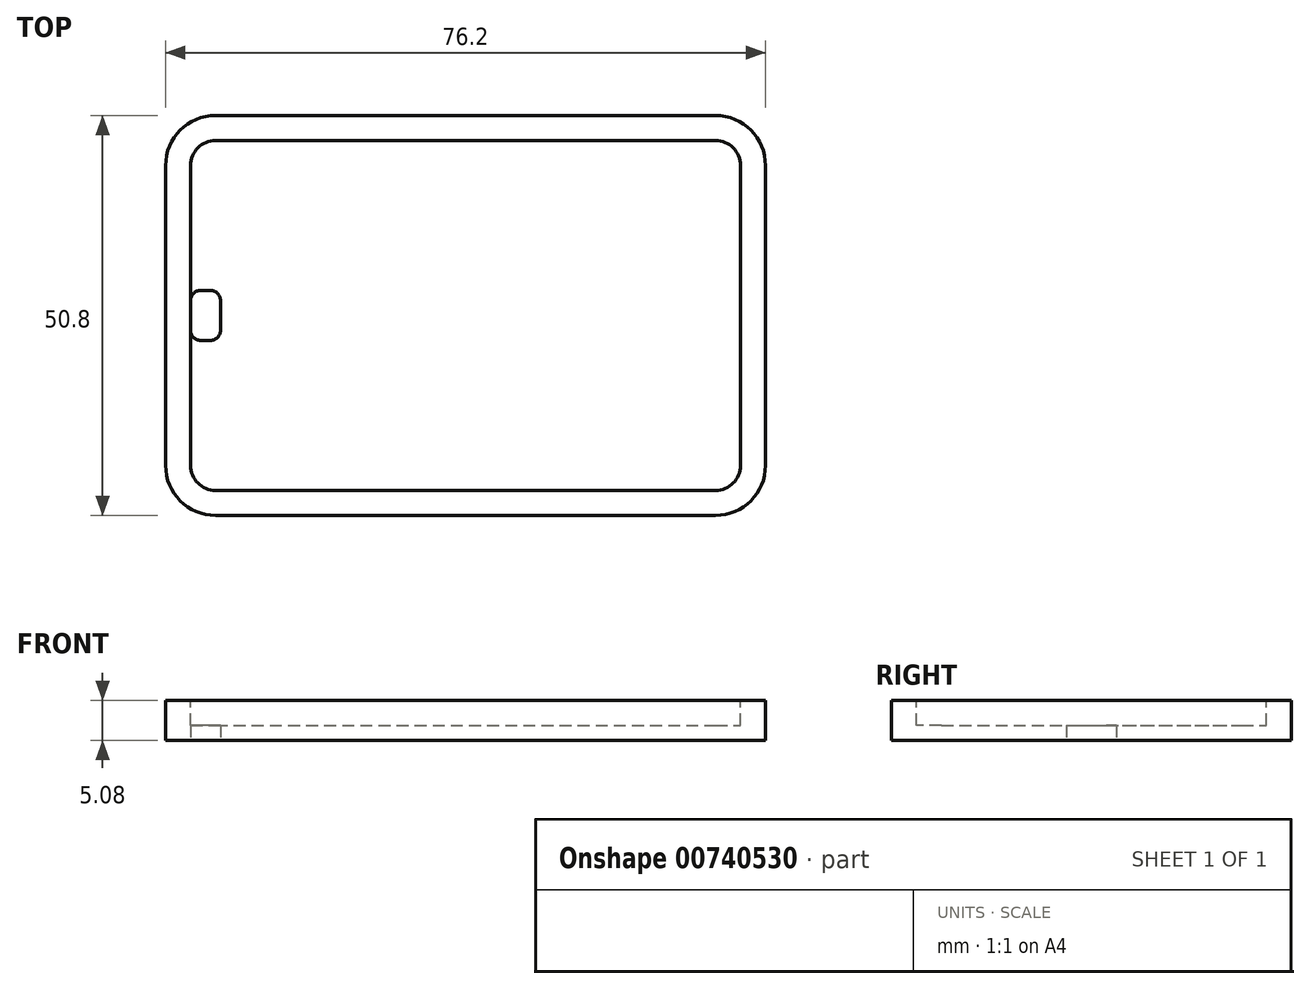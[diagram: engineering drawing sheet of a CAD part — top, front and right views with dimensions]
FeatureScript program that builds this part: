
annotation { "Feature Type Name" : "Feature", "Feature Type Description" : "" }
export const myFeature = defineFeature(function(context is Context, id is Id, definition is map)
    precondition{}
    {
        {
            var Q0;
            Q0=qCreatedBy(makeId("Top.planeOp"),FACE);
            var sketch = newSketch(context, id + "F0", { "sketchPlane" : qUnion([Q0])});
            skLineSegment(sketch, "E0.bottom", {"start": v(6.35, 0) * mm, "end": v(69.85, 0) * mm});
            skLineSegment(sketch, "E0.top", {"start": v(6.35, 50.8) * mm, "end": v(69.85, 50.8) * mm});
            skLineSegment(sketch, "E0.left", {"start": v(0, 6.35) * mm, "end": v(0, 44.45) * mm});
            skLineSegment(sketch, "E0.right", {"start": v(76.2, 6.35) * mm, "end": v(76.2, 44.45) * mm});
            skPoint(sketch, "E1.visualSharp", {"position": v(0, 50.8) * mm});
            skArc(sketch, "E1.filletArc", {"start": v(6.35, 50.8) * mm, "mid": v(1.86, 48.94) * mm, "end": v(0, 44.45) * mm});
            skPoint(sketch, "E2.visualSharp", {"position": v(76.2, 50.8) * mm});
            skArc(sketch, "E2.filletArc", {"start": v(76.2, 44.45) * mm, "mid": v(74.34, 48.94) * mm, "end": v(69.85, 50.8) * mm});
            skPoint(sketch, "E3.visualSharp", {"position": v(0, 0) * mm});
            skArc(sketch, "E3.filletArc", {"start": v(0, 6.35) * mm, "mid": v(1.86, 1.86) * mm, "end": v(6.35, 0) * mm});
            skPoint(sketch, "E4.visualSharp", {"position": v(76.2, 0) * mm});
            skArc(sketch, "E4.filletArc", {"start": v(69.85, 0) * mm, "mid": v(74.34, 1.86) * mm, "end": v(76.2, 6.35) * mm});
            skSolve(sketch);
        }
        {
            var Q0;
            Q0 = qSketchRegion(id + "F0", true);
            extrude(context, id + "F1", {"entities" : qUnion([Q0]), "depth" : 5.08 * mm, "offsetDistance" : 25.4 * mm});
        }
        {
            var Q0;
            Q0=makeQuery(id+"F1.opExtrude","CAP_FACE",FACE,{"disambiguationData":[OSD([sQuery(id+"F0.wireOp",EDGE,"E0.bottom"),sQuery(id+"F0.wireOp",EDGE,"E0.top"),sQuery(id+"F0.wireOp",EDGE,"E0.left"),sQuery(id+"F0.wireOp",EDGE,"E0.right"),sQuery(id+"F0.wireOp",EDGE,"E1.filletArc"),sQuery(id+"F0.wireOp",EDGE,"E2.filletArc"),sQuery(id+"F0.wireOp",EDGE,"E3.filletArc"),sQuery(id+"F0.wireOp",EDGE,"E4.filletArc")])],"isStart":false});
            var sketch = newSketch(context, id + "F2", { "sketchPlane" : qUnion([Q0])});
            skLineSegment(sketch, "E5.0", {"start": v(6.35, 47.63) * mm, "end": v(69.85, 47.63) * mm});
            skLineSegment(sketch, "E5.1", {"start": v(3.17, 6.35) * mm, "end": v(3.17, 44.45) * mm});
            skLineSegment(sketch, "E5.2", {"start": v(6.35, 3.17) * mm, "end": v(69.85, 3.17) * mm});
            skLineSegment(sketch, "E5.3", {"start": v(73.03, 6.35) * mm, "end": v(73.03, 44.45) * mm});
            skPoint(sketch, "E6.visualSharp", {"position": v(3.17, 47.63) * mm});
            skArc(sketch, "E6.filletArc", {"start": v(6.35, 47.63) * mm, "mid": v(4.1, 46.7) * mm, "end": v(3.17, 44.45) * mm});
            skPoint(sketch, "E7.visualSharp", {"position": v(3.17, 3.17) * mm});
            skArc(sketch, "E7.filletArc", {"start": v(3.17, 6.35) * mm, "mid": v(4.1, 4.1) * mm, "end": v(6.35, 3.17) * mm});
            skPoint(sketch, "E8.visualSharp", {"position": v(73.03, 3.17) * mm});
            skArc(sketch, "E8.filletArc", {"start": v(69.85, 3.17) * mm, "mid": v(72.1, 4.1) * mm, "end": v(73.03, 6.35) * mm});
            skPoint(sketch, "E9.visualSharp", {"position": v(73.03, 47.63) * mm});
            skArc(sketch, "E9.filletArc", {"start": v(73.02, 44.45) * mm, "mid": v(72.1, 46.7) * mm, "end": v(69.85, 47.63) * mm});
            skSolve(sketch);
        }
        {
            var Q0;
            Q0 = qSketchRegion(id + "F2", true);
            extrude(context, id + "F3", {"entities" : qUnion([Q0]), "operationType" : NewBodyOperationType.REMOVE, "oppositeDirection" : true, "depth" : 3.17 * mm, "offsetDistance" : 25.4 * mm});
        }
        {
            var Q0;
            Q0=qCreatedBy(makeId("Top.planeOp"),FACE);
            var sketch = newSketch(context, id + "F4", { "sketchPlane" : qUnion([Q0])});
            skLineSegment(sketch, "E10.bottom", {"start": v(4.45, 28.58) * mm, "end": v(5.7, 28.58) * mm});
            skLineSegment(sketch, "E10.top", {"start": v(4.45, 22.23) * mm, "end": v(5.7, 22.23) * mm});
            skLineSegment(sketch, "E10.left", {"start": v(3.18, 27.3) * mm, "end": v(3.18, 23.5) * mm});
            skLineSegment(sketch, "E10.right", {"start": v(6.98, 27.3) * mm, "end": v(6.98, 23.5) * mm});
            skLineSegment(sketch, "E11", {"start": v(13.59, 25.4) * mm, "end": v(-6, 25.4) * mm, "construction": true});
            skPoint(sketch, "E12.visualSharp", {"position": v(6.98, 28.58) * mm});
            skArc(sketch, "E12.filletArc", {"start": v(6.98, 27.3) * mm, "mid": v(6.6, 28.2) * mm, "end": v(5.7, 28.58) * mm});
            skPoint(sketch, "E13.visualSharp", {"position": v(3.17, 28.58) * mm});
            skArc(sketch, "E13.filletArc", {"start": v(4.45, 28.58) * mm, "mid": v(3.55, 28.2) * mm, "end": v(3.18, 27.3) * mm});
            skPoint(sketch, "E14.visualSharp", {"position": v(6.98, 22.23) * mm});
            skArc(sketch, "E14.filletArc", {"start": v(5.7, 22.23) * mm, "mid": v(6.6, 22.6) * mm, "end": v(6.98, 23.5) * mm});
            skPoint(sketch, "E15.visualSharp", {"position": v(3.17, 22.23) * mm});
            skArc(sketch, "E15.filletArc", {"start": v(3.18, 23.5) * mm, "mid": v(3.55, 22.6) * mm, "end": v(4.45, 22.23) * mm});
            skSolve(sketch);
        }
        {
            var Q0;
            Q0 = qSketchRegion(id + "F4", true);
            extrude(context, id + "F5", {"entities" : qUnion([Q0]), "operationType" : NewBodyOperationType.REMOVE, "oppositeDirection" : true, "depth" : -25.4 * mm, "offsetDistance" : 25.4 * mm});
        }
    });
